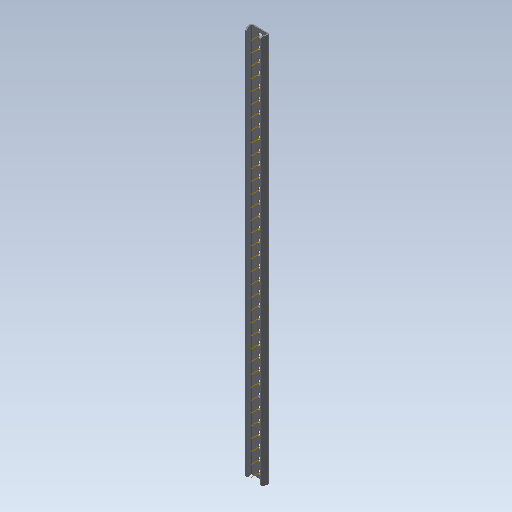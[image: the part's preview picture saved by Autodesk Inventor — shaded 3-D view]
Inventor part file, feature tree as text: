
AUTODESK INVENTOR PART (.ipt)
format: ipt  version: 2020 (Build 240168000, 168)  size: 461,312 bytes
history: native  units: in
note: dims shown in document units (in); Inventor stores cm internally (conversion verified against a paired STEP export)
features: other x39, boolean_combine x1, extrude x1, pattern_linear x1, imported_body x1, sketch x1
ambient origin geometry x8: Origin, YZ Plane, XZ Plane, XY Plane, X Axis, Y Axis, Z Axis, Center Point
bodies: Body1 (feature_tree)
feature tree (44):
  boolean_combine  "Combine1"
  other  "Linear Slide"
  other  "Work Axis1"
  extrude  "Extrusion1"  TaperAngle=0.0deg  [1 undecoded]
  pattern_linear  "Rectangular Pattern1"  Spacing1=0.0in  [1 undecoded]
  other  "bottom plane"
  other  "top plane"
  imported_body  "Base1"
  other  "Work Point1"
  other  "Work Axis2"
  sketch  "Sketch1"  dims[d0=13.7795in d2=0.5in d4=0.0in d5=0.0in d6=0.0in d8=0.0in]
  other  "Work Axis46"
  other  "Work Axis47"
  other  "Work Axis48"
  other  "Work Axis49"
  other  "Work Axis50"
  other  "Work Axis51"
  other  "Work Axis52"
  other  "Work Axis53"
  other  "Work Axis54"
  other  "Work Axis55"
  other  "Work Axis56"
  other  "Work Axis57"
  other  "Work Axis69"
  other  "Work Axis70"
  other  "Work Axis71"
  other  "Work Axis72"
  other  "Work Axis73"
  other  "Work Axis74"
  other  "Work Axis75"
  other  "Work Axis76"
  other  "Work Axis77"
  other  "Work Axis78"
  other  "Work Axis90"
  other  "Work Axis91"
  other  "Work Axis92"
  other  "Work Axis93"
  other  "Work Axis94"
  other  "Work Axis95"
  other  "Work Axis96"
  other  "Work Axis97"
  other  "Work Axis98"
  other  "Work Axis99"
  other  "Work Axis100"
note: 2 required parameter values undecoded (feature->parameter linkage not recoverable at this tier; creation-order binding heuristic only, values carry confidence <= 0.55)
